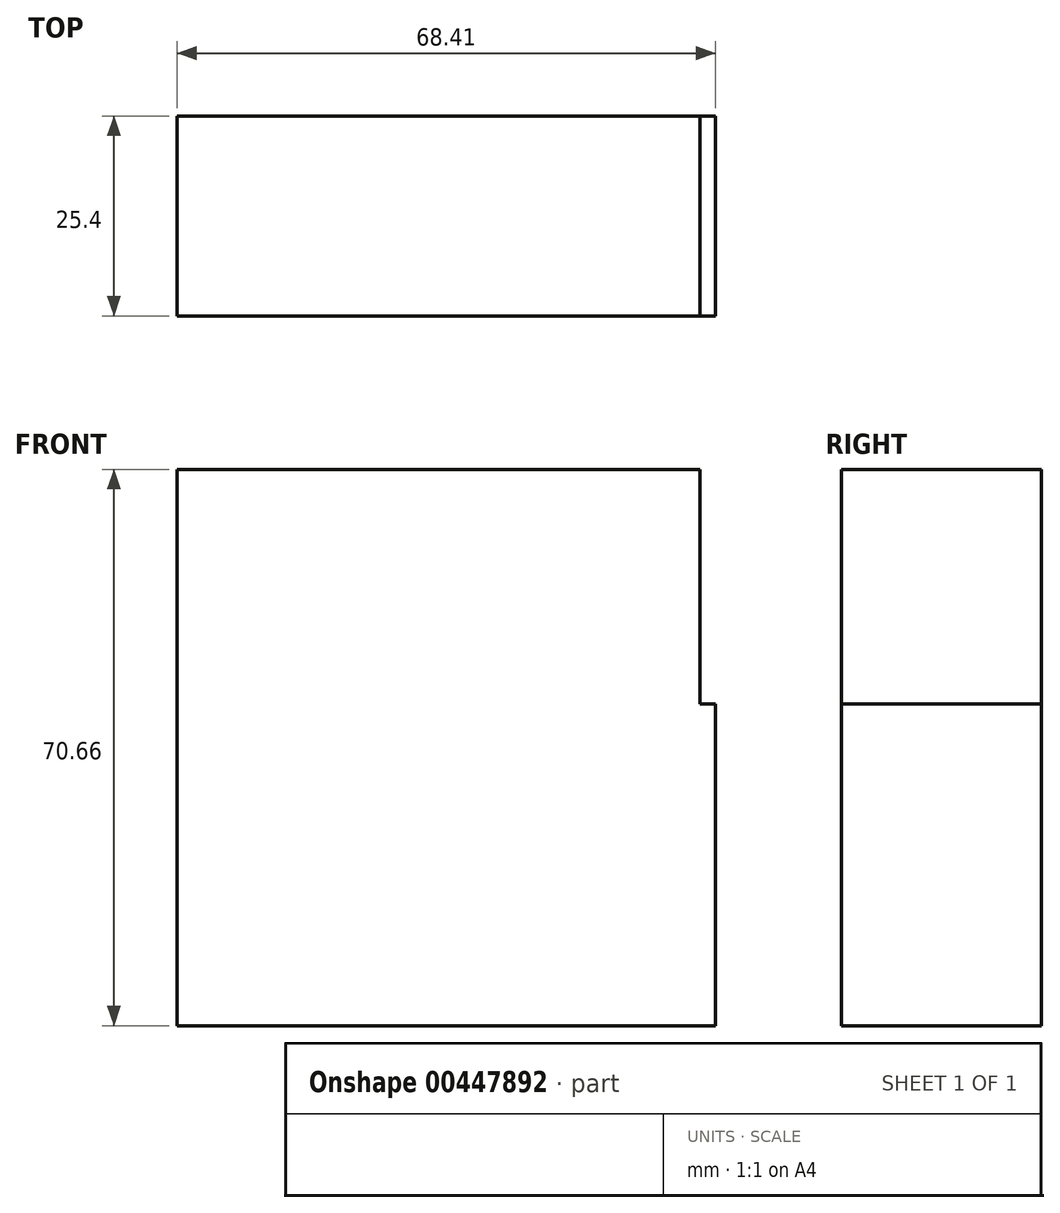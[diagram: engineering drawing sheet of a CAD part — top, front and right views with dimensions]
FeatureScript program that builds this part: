
annotation { "Feature Type Name" : "Feature", "Feature Type Description" : "" }
export const myFeature = defineFeature(function(context is Context, id is Id, definition is map)
    precondition{}
    {
        {
            var Q0;
            Q0=qCreatedBy(makeId("Front.planeOp"),FACE);
            var sketch = newSketch(context, id + "F0", { "sketchPlane" : qUnion([Q0])});
            skLineSegment(sketch, "E0.bottom", {"start": v(-39.78, 51.32) * mm, "end": v(28.63, 51.32) * mm});
            skLineSegment(sketch, "E0.top", {"start": v(-39.78, -19.34) * mm, "end": v(28.63, -19.34) * mm});
            skLineSegment(sketch, "E0.left", {"start": v(-39.78, 51.32) * mm, "end": v(-39.78, -19.34) * mm});
            skLineSegment(sketch, "E0.right", {"start": v(28.63, 51.32) * mm, "end": v(28.63, -19.34) * mm});
            skLineSegment(sketch, "E1.bottom", {"start": v(28.63, 51.32) * mm, "end": v(28.63, 51.32) * mm});
            skLineSegment(sketch, "E1.top", {"start": v(28.63, 23.87) * mm, "end": v(28.63, 23.87) * mm});
            skLineSegment(sketch, "E1.left", {"start": v(28.63, 51.32) * mm, "end": v(28.63, 23.87) * mm});
            skLineSegment(sketch, "E1.right", {"start": v(28.63, 51.32) * mm, "end": v(28.63, 23.87) * mm});
            skPoint(sketch, "E1.middle", {"position": v(28.63, 37.6) * mm});
            skLineSegment(sketch, "E2.bottom", {"start": v(60.32, 53.67) * mm, "end": v(26.68, 53.67) * mm});
            skLineSegment(sketch, "E2.top", {"start": v(60.32, 21.52) * mm, "end": v(26.68, 21.52) * mm});
            skLineSegment(sketch, "E2.left", {"start": v(60.32, 53.67) * mm, "end": v(60.32, 21.52) * mm});
            skLineSegment(sketch, "E2.right", {"start": v(26.68, 53.67) * mm, "end": v(26.68, 21.52) * mm});
            skPoint(sketch, "E2.middle", {"position": v(43.5, 37.6) * mm});
            skSolve(sketch);
        }
        {
            var Q0;
            {var subQ1=sQuery(id+"F0.wireOp",EDGE,"E0.top");Q0=makeQuery(id+"F0.imprint","IMPRINT",FACE,{"disambiguationData":[TD([[makeQuery(id+"F0.imprint","IMPRINT",EDGE,{"derivedFrom":subQ1}),1.0]])]});}
            extrude(context, id + "F1", {"entities" : qUnion([Q0]), "depth" : 25.4 * mm});
        }
    });
